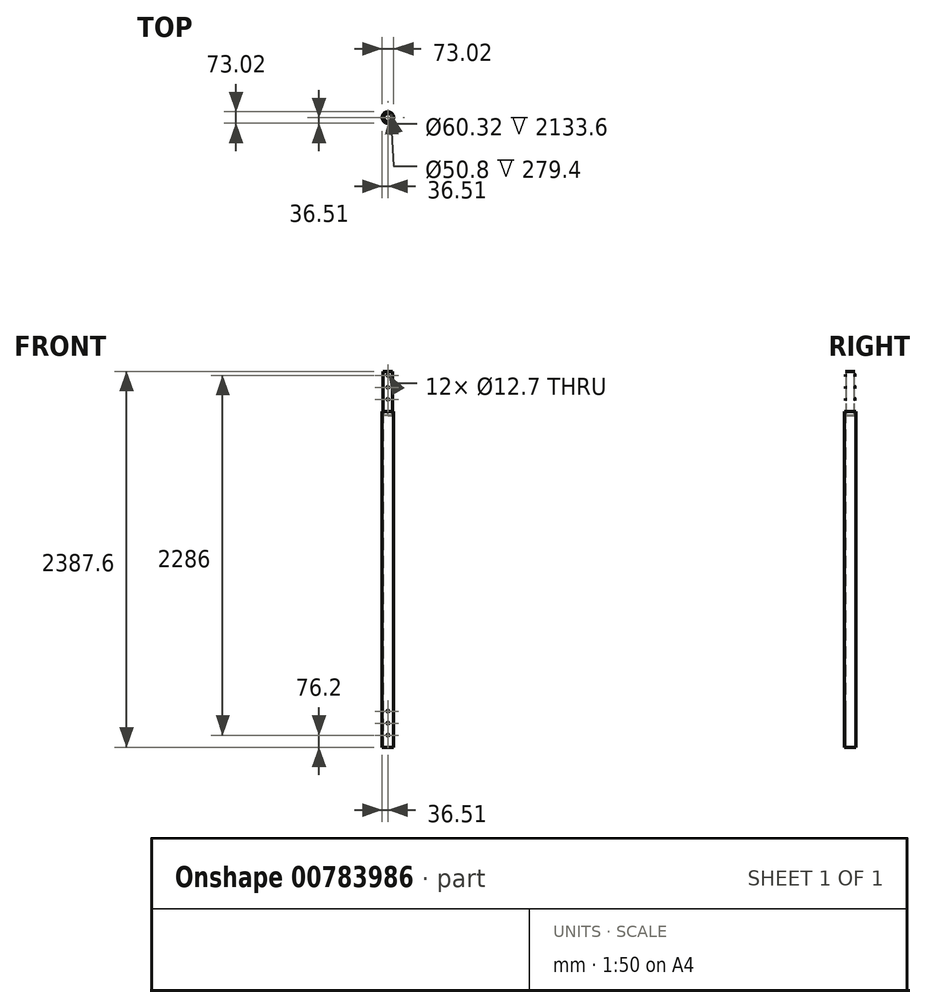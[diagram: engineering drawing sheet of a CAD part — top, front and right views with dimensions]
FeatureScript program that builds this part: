
annotation { "Feature Type Name" : "Feature", "Feature Type Description" : "" }
export const myFeature = defineFeature(function(context is Context, id is Id, definition is map)
    precondition{}
    {
        {
            var Q0;
            Q0=qCreatedBy(makeId("Top.planeOp"),FACE);
            var sketch = newSketch(context, id + "F0", { "sketchPlane" : qUnion([Q0])});
            skCircle(sketch, "E0", {"center": v(0, 0) * mm, "radius": 30.16 * mm});
            skCircle(sketch, "E1", {"center": v(0, 0) * mm, "radius": 36.51 * mm});
            skSolve(sketch);
        }
        {
            var Q0;
            Q0=makeQuery(id+"F0.imprint","IMPRINT",FACE,{"disambiguationData":[TD([[makeQuery(id+"F0.imprint","IMPRINT",EDGE,{"derivedFrom":sQuery(id+"F0.wireOp",EDGE,"E0")}),-1.0]])]});
            extrude(context, id + "F1", {"entities" : qUnion([Q0]), "depth" : 2133.6 * mm, "offsetDistance" : 25.4 * mm});
        }
        {
            var Q0;
            Q0=qCreatedBy(makeId("Top.planeOp"),FACE);
            var sketch = newSketch(context, id + "F2", { "sketchPlane" : qUnion([Q0])});
            skLineSegment(sketch, "E2.bottom", {"start": v(-36.5, 0) * mm, "end": v(36.53, 0) * mm});
            skLineSegment(sketch, "E2.top", {"start": v(-36.5, -36.53) * mm, "end": v(36.53, -36.53) * mm});
            skLineSegment(sketch, "E2.left", {"start": v(-36.5, 0) * mm, "end": v(-36.5, -36.53) * mm});
            skLineSegment(sketch, "E2.right", {"start": v(36.53, 0) * mm, "end": v(36.53, -36.53) * mm});
            skSolve(sketch);
        }
        {
            var Q0;
            Q0=sQuery(id+"F2.wireOp",EDGE,"E2.bottom");
            cPlane(context, id + "F3", {"entities" : qUnion([Q0]), "cplaneType" : CPlaneType.LINE_ANGLE, "offset" : 25.4 * mm, "angle" : 0 * degree, "width" : 152.4 * mm, "height" : 152.4 * mm});
        }
        {
            var Q0;
            Q0=qCreatedBy(id+"F3.planeOp",FACE);
            var sketch = newSketch(context, id + "F4", { "sketchPlane" : qUnion([Q0])});
            skCircle(sketch, "E3", {"center": v(0, 76.2) * mm, "radius": 6.35 * mm});
            skCircle(sketch, "E4", {"center": v(0, 152.4) * mm, "radius": 6.35 * mm});
            skCircle(sketch, "E5", {"center": v(0, 228.6) * mm, "radius": 6.35 * mm});
            skLineSegment(sketch, "E6", {"start": v(134.12, 152.4) * mm, "end": v(-322.93, 152.4) * mm, "construction": true});
            skLineSegment(sketch, "E7", {"start": v(162.25, 1740.17) * mm, "end": v(-247.1, 1740.17) * mm, "construction": true});
            skSolve(sketch);
        }
        {
            var Q0;
            Q0=qSketchRegion(id+"F4",true);
            extrude(context, id + "F5", {"entities" : qUnion([Q0]), "operationType" : NewBodyOperationType.REMOVE, "oppositeDirection" : true, "depth" : 50.8 * mm, "offsetDistance" : 25.4 * mm, "hasSecondDirection" : true, "secondDirectionOppositeDirection" : false, "secondDirectionDepth" : 50.8 * mm});
        }
        {
            var Q0;
            Q0=qCreatedBy(makeId("Front.planeOp"),FACE);
            var sketch = newSketch(context, id + "F6", { "sketchPlane" : qUnion([Q0])});
            skLineSegment(sketch, "E8", {"start": v(0, 0) * mm, "end": v(0, 6747.37) * mm, "construction": true});
            skSolve(sketch);
        }
        {
            var Q0;
            Q0=makeQuery(id+"F1.opExtrude","CAP_FACE",FACE,{"disambiguationData":[OSD([sQuery(id+"F0.wireOp",EDGE,"E0"),sQuery(id+"F0.wireOp",EDGE,"E1")])],"isStart":false});
            var sketch = newSketch(context, id + "F7", { "sketchPlane" : qUnion([Q0])});
            skCircle(sketch, "E9", {"center": v(0, 0) * mm, "radius": 25.4 * mm});
            skCircle(sketch, "E10", {"center": v(0.01, 0) * mm, "radius": 30.16 * mm});
            skSolve(sketch);
        }
        {
            var Q0;
            Q0=makeQuery(id+"F7.imprint","IMPRINT",FACE,{"disambiguationData":[TD([[makeQuery(id+"F7.imprint","IMPRINT",EDGE,{"derivedFrom":sQuery(id+"F7.wireOp",EDGE,"E9")}),-1.0]])]});
            extrude(context, id + "F8", {"entities" : qUnion([Q0]), "operationType" : NewBodyOperationType.ADD, "oppositeDirection" : true, "depth" : 25.4 * mm, "offsetDistance" : 25.4 * mm, "hasSecondDirection" : true, "secondDirectionOppositeDirection" : false, "secondDirectionDepth" : 254 * mm});
        }
        {
            var Q0;
            Q0=qCreatedBy(makeId("Front.planeOp"),FACE);
            var sketch = newSketch(context, id + "F9", { "sketchPlane" : qUnion([Q0])});
            skCircle(sketch, "E11", {"center": v(0, 2209.8) * mm, "radius": 6.35 * mm});
            skCircle(sketch, "E12", {"center": v(0, 2286) * mm, "radius": 6.35 * mm});
            skCircle(sketch, "E13", {"center": v(0, 2362.2) * mm, "radius": 6.35 * mm});
            skSolve(sketch);
        }
        {
            var Q0;
            Q0 = qSketchRegion(id + "F9", true);
            extrude(context, id + "F10", {"entities" : qUnion([Q0]), "operationType" : NewBodyOperationType.REMOVE, "oppositeDirection" : true, "depth" : 50.8 * mm, "offsetDistance" : 25.4 * mm, "hasSecondDirection" : true, "secondDirectionOppositeDirection" : false, "secondDirectionDepth" : 50.8 * mm});
        }
    });
